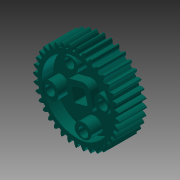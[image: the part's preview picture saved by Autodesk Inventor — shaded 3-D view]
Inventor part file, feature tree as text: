
AUTODESK INVENTOR PART (.ipt)
format: ipt  version: 2013 (Build 170138000, 138)  size: 571,904 bytes
history: native  units: in
note: dims shown in document units (in); Inventor stores cm internally (conversion verified against a paired STEP export)
features: extrude x7, sketch x5, plane x3, other x1, projected_geometry x1
ambient origin geometry x8: Origin, YZ Plane, XZ Plane, XY Plane, X Axis, Y Axis, Z Axis, Center Point
bodies: Solid1 (feature_tree)
feature tree (17):
  sketch  "Sketch1"  dims[d0=0.5in d1=0.0in d2=0.086in d3=0.0in]
  extrude  "Extrusion1"  Depth=0.086in TaperAngle=0.0deg
  plane  "Work Plane1"
  extrude  "Extrusion2"  [1 undecoded]
  extrude  "Extrusion3"  Depth=0.086in TaperAngle=0.0deg
  plane  "Work Plane2"
  plane  "Work Plane3"
  extrude  "Extrusion4"  Depth=0.086in TaperAngle=0.0deg
  extrude  "Extrusion5"  TaperAngle=0.0deg  [1 undecoded]
  sketch  "Sketch3"  dims[d7=-0.0579in d8=0.086in d9=0.0in]
  extrude  "Extrusion6"  TaperAngle=0.0deg  [1 undecoded]
  sketch  "Sketch2"  dims[d4=0.086in d5=0.0in d6=-0.0579in]
  sketch  "Sketch4"  dims[d10=0.086in d11=0.0in d12=0.086in d13=0.0in]
  sketch  "Sketch5"  dims[d14=0.3515in d15=0.0in d16=0.0in d17=0.0in]
  other  "Srf1"
  extrude  "ExtrusionSrf1"  [1 undecoded]
  projected_geometry  "Project Cut Edges1"
note: 4 required parameter values undecoded (feature->parameter linkage not recoverable at this tier; creation-order binding heuristic only, values carry confidence <= 0.55)
